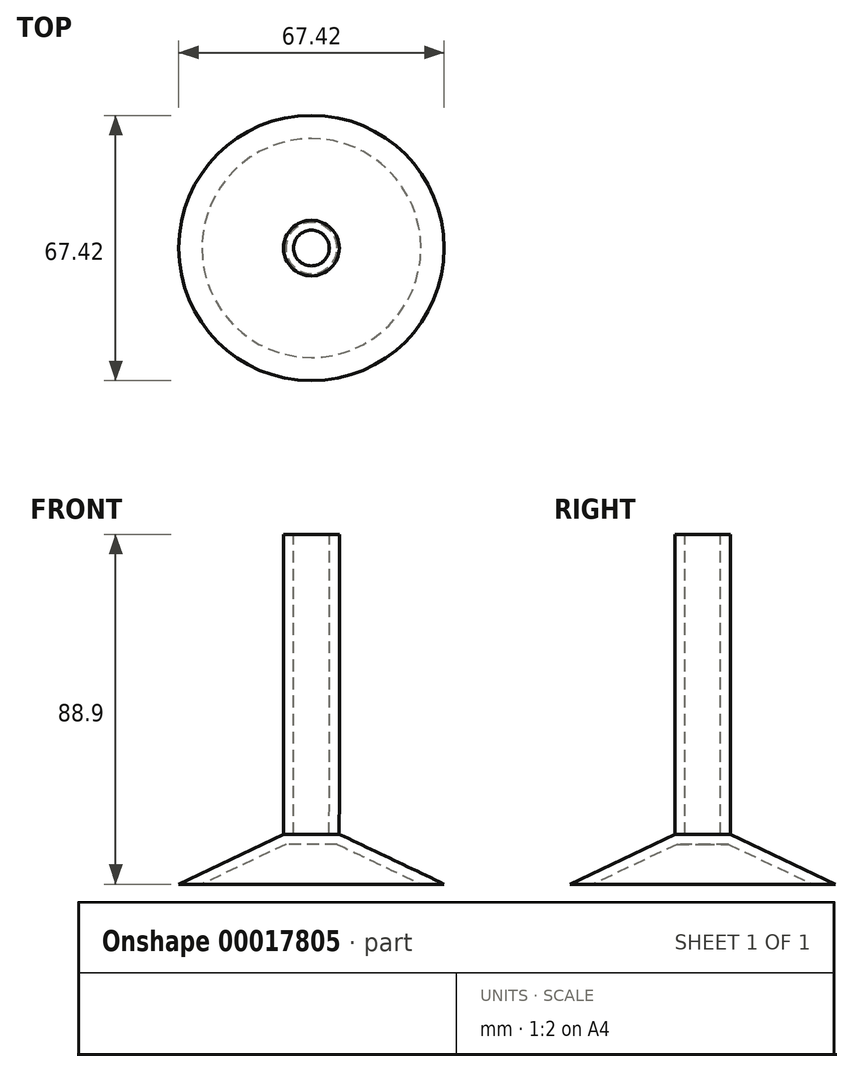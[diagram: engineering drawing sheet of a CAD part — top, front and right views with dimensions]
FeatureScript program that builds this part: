
annotation { "Feature Type Name" : "Feature", "Feature Type Description" : "" }
export const myFeature = defineFeature(function(context is Context, id is Id, definition is map)
    precondition{}
    {
        {
            var Q0;
            Q0=qCreatedBy(makeId("Top.planeOp"),FACE);
            var sketch = newSketch(context, id + "F0", { "sketchPlane" : qUnion([Q0])});
            skCircle(sketch, "E0", {"center": v(0, 0) * mm, "radius": 33.71 * mm});
            skSolve(sketch);
        }
        {
            var Q0;
            Q0=qCreatedBy(makeId("Top.planeOp"),FACE);
            cPlane(context, id + "F1", {"entities" : qUnion([Q0]), "cplaneType" : CPlaneType.OFFSET, "offset" : 12.7 * mm, "width" : 152.4 * mm, "height" : 152.4 * mm});
        }
        {
            var Q0;
            Q0=qCreatedBy(id+"F1.planeOp",FACE);
            var sketch = newSketch(context, id + "F2", { "sketchPlane" : qUnion([Q0])});
            skPoint(sketch, "E1.0", {"position": v(0, 0) * mm});
            skSolve(sketch);
        }
        {
            var Q0;
            Q0=qCreatedBy(id+"F1.planeOp",FACE);
            var sketch = newSketch(context, id + "F3", { "sketchPlane" : qUnion([Q0])});
            skCircle(sketch, "E2", {"center": v(0, 0) * mm, "radius": 7.07 * mm});
            skSolve(sketch);
        }
        {
            var Q0;
            Q0=makeQuery(id+"F0.imprint","IMPRINT",FACE,{"disambiguationData":[TD([[makeQuery(id+"F0.imprint","IMPRINT",EDGE,{"derivedFrom":sQuery(id+"F0.wireOp",EDGE,"E0")}),1.0]])]});
            var Q1;
            Q1=makeQuery(id+"F3.imprint","IMPRINT",FACE,{"disambiguationData":[TD([[makeQuery(id+"F3.imprint","IMPRINT",EDGE,{"derivedFrom":sQuery(id+"F3.wireOp",EDGE,"E2")}),1.0]])]});
            loft(context, id + "F4", {"sheetProfilesArray" : [{ "sheetProfileEntities" : qUnion([Q0]) }, { "sheetProfileEntities" : qUnion([Q1]) }]});
        }
        {
            var Q0;
            Q0=makeQuery(id+"F4.opLoft","CAP_FACE",FACE,{"disambiguationData":[OSD([makeQuery(id+"F0.imprint","IMPRINT",FACE,{"disambiguationData":[TD([[makeQuery(id+"F0.imprint","IMPRINT",EDGE,{"derivedFrom":sQuery(id+"F0.wireOp",EDGE,"E0")}),1.0]])]})])],"isStart":true});
            shell(context, id + "F5", {"entities" : qUnion([Q0]), "thickness" : 2.54 * mm});
        }
        {
            var Q0;
            Q0=qCreatedBy(id+"F1.planeOp",FACE);
            cPlane(context, id + "F6", {"entities" : qUnion([Q0]), "cplaneType" : CPlaneType.OFFSET, "offset" : 76.2 * mm, "width" : 152.4 * mm, "height" : 152.4 * mm});
        }
        {
            var Q0;
            Q0=qCreatedBy(id+"F6.planeOp",FACE);
            var sketch = newSketch(context, id + "F7", { "sketchPlane" : qUnion([Q0])});
            skPoint(sketch, "E3.0", {"position": v(0, 0) * mm});
            skCircle(sketch, "E4", {"center": v(0, 0) * mm, "radius": 7.07 * mm});
            skSolve(sketch);
        }
        {
            var Q1;
            Q1=makeQuery(id+"F3.imprint","IMPRINT",FACE,{"disambiguationData":[TD([[makeQuery(id+"F3.imprint","IMPRINT",EDGE,{"derivedFrom":sQuery(id+"F3.wireOp",EDGE,"E2")}),1.0]])]});
            var Q2;
            Q2=makeQuery(id+"F7.imprint","IMPRINT",FACE,{"disambiguationData":[TD([[makeQuery(id+"F7.imprint","IMPRINT",EDGE,{"derivedFrom":sQuery(id+"F7.wireOp",EDGE,"E4")}),1.0]])]});
            loft(context, id + "F8", {"operationType" : NewBodyOperationType.ADD, "sheetProfilesArray" : [{ "sheetProfileEntities" : qUnion([Q1]) }, { "sheetProfileEntities" : qUnion([Q2]) }]});
        }
        {
            var Q0;
            Q0=makeQuery(id+"F8.opLoft","CAP_FACE",FACE,{"disambiguationData":[OSD([makeQuery(id+"F7.imprint","IMPRINT",FACE,{"disambiguationData":[TD([[makeQuery(id+"F7.imprint","IMPRINT",EDGE,{"derivedFrom":sQuery(id+"F7.wireOp",EDGE,"E4")}),1.0]])]})])],"isStart":true});
            shell(context, id + "F9", {"entities" : qUnion([Q0]), "thickness" : 2.54 * mm});
        }
    });
